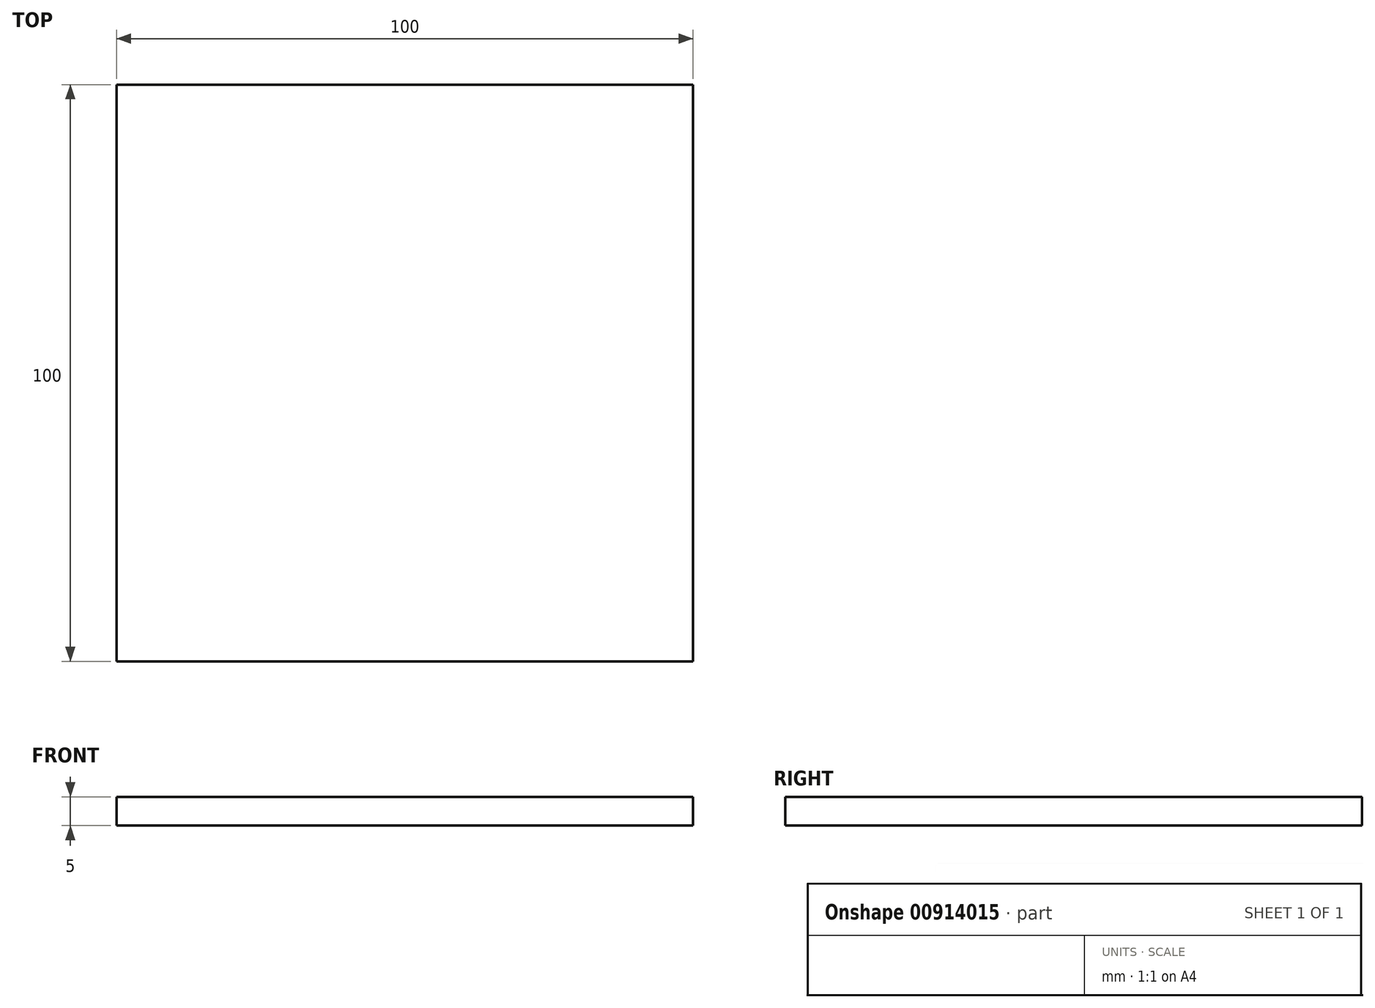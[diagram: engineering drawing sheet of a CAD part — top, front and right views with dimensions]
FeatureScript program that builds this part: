
annotation { "Feature Type Name" : "Feature", "Feature Type Description" : "" }
export const myFeature = defineFeature(function(context is Context, id is Id, definition is map)
    precondition{}
    {
        {
            var Q0;
            Q0=qCreatedBy(makeId("Top.planeOp"),FACE);
            var sketch = newSketch(context, id + "F0", { "sketchPlane" : qUnion([Q0])});
            skCircle(sketch, "E0.cCircle", {"center": v(0, 0) * mm, "radius": 50 * mm, "construction": true});
            skLineSegment(sketch, "E0.0", {"start": v(50, 50) * mm, "end": v(50, -50) * mm});
            skLineSegment(sketch, "E0.1", {"start": v(50, -50) * mm, "end": v(-50, -50) * mm});
            skLineSegment(sketch, "E0.2", {"start": v(-50, -50) * mm, "end": v(-50, 50) * mm});
            skLineSegment(sketch, "E0.3", {"start": v(-50, 50) * mm, "end": v(50, 50) * mm});
            skPoint(sketch, "E0.0.midPoint", {"position": v(50, 0) * mm});
            skSolve(sketch);
        }
        {
            var Q0;
            Q0=makeQuery(id+"F0.imprint","IMPRINT",FACE,{"disambiguationData":[TD([[makeQuery(id+"F0.imprint","IMPRINT",EDGE,{"derivedFrom":sQuery(id+"F0.wireOp",EDGE,"E0.0")}),-1.0]])]});
            extrude(context, id + "F1", {"entities" : qUnion([Q0]), "depth" : 5 * mm, "offsetDistance" : 25 * mm});
        }
    });
